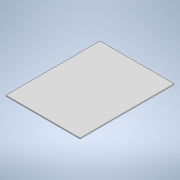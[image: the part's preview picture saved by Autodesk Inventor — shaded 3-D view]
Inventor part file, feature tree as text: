
AUTODESK INVENTOR PART (.ipt)
format: ipt  version: 2022 (Build 260153000, 153)  size: 90,624 bytes
history: native  units: in
note: dims shown in document units (in); Inventor stores cm internally (conversion verified against a paired STEP export)
features: extrude x1, sketch x1
ambient origin geometry x8: Origin, YZ Plane, XZ Plane, XY Plane, X Axis, Y Axis, Z Axis, Center Point
bodies: Solid1 (feature_tree)
feature tree (2):
  extrude  "Extrusion1"  Depth=20.4724in
  sketch  "Sketch1"  dims[d0=16.1417in d1=20.4724in d2=0.1969in d3=0.0in]
